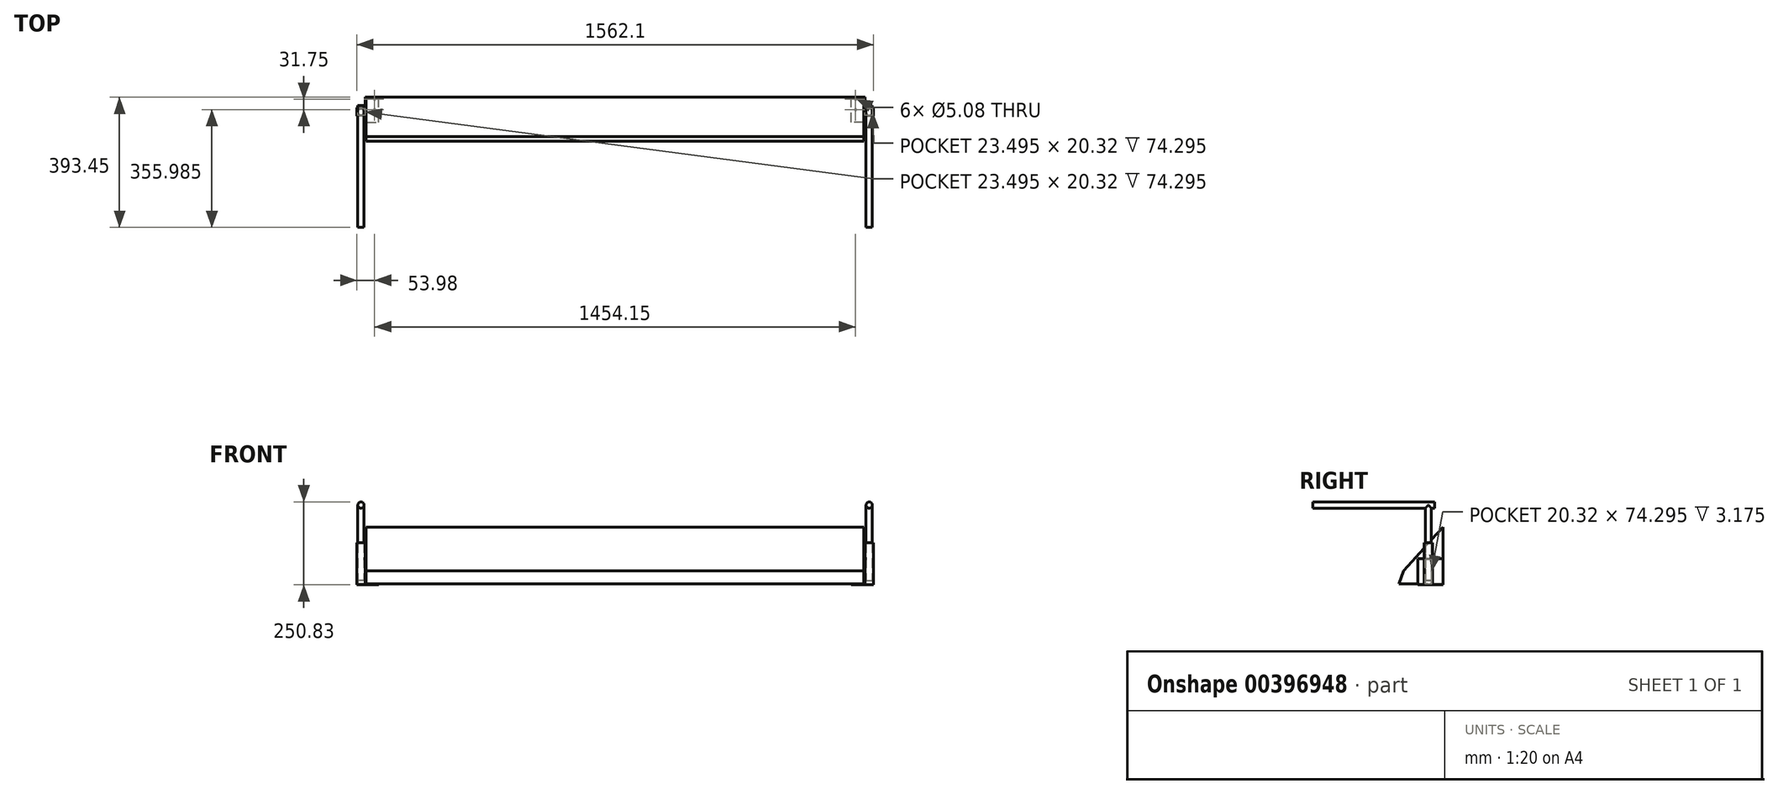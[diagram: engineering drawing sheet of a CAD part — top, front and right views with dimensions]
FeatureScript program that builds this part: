
annotation { "Feature Type Name" : "Feature", "Feature Type Description" : "" }
export const myFeature = defineFeature(function(context is Context, id is Id, definition is map)
    precondition{}
    {
        {
            var Q0;
            Q0=qCreatedBy(makeId("Right.planeOp"),FACE);
            var sketch = newSketch(context, id + "F0", { "sketchPlane" : qUnion([Q0])});
            skLineSegment(sketch, "E0", {"start": v(0, 0) * mm, "end": v(0, 171.45) * mm});
            skLineSegment(sketch, "E1", {"start": v(0, 0) * mm, "end": v(-133.35, 0) * mm});
            skLineSegment(sketch, "E2", {"start": v(-133.35, 0) * mm, "end": v(-119.18, 39.5) * mm});
            skLineSegment(sketch, "E3", {"start": v(-119.18, 39.5) * mm, "end": v(0, 171.45) * mm});
            skSolve(sketch);
        }
        {
            var Q0;
            Q0=makeQuery(id+"F0.imprint","IMPRINT",FACE,{"disambiguationData":[TD([[makeQuery(id+"F0.imprint","IMPRINT",EDGE,{"derivedFrom":sQuery(id+"F0.wireOp",EDGE,"E0")}),1.0]])]});
            extrude(context, id + "F1", {"entities" : qUnion([Q0]), "oppositeDirection" : true, "depth" : 1504.95 * mm});
        }
        {
            var Q0;
            Q0=makeQuery(id+"F1.opExtrude","SWEPT_FACE",FACE,{"disambiguationData":[OSD([sQuery(id+"F0.wireOp",EDGE,"E1")])]});
            var sketch = newSketch(context, id + "F2", { "sketchPlane" : qUnion([Q0])});
            skCircle(sketch, "E4", {"center": v(-1479.55, 37.46) * mm, "radius": 2.54 * mm});
            skCircle(sketch, "E5", {"center": v(-1479.55, 5.72) * mm, "radius": 2.54 * mm});
            skLineSegment(sketch, "E6.bottom", {"start": v(-1504.95, 76.2) * mm, "end": v(-1466.85, 76.2) * mm});
            skLineSegment(sketch, "E6.top", {"start": v(-1504.95, 0) * mm, "end": v(-1466.85, 0) * mm});
            skLineSegment(sketch, "E6.left", {"start": v(-1504.95, 76.2) * mm, "end": v(-1504.95, 0) * mm});
            skLineSegment(sketch, "E6.right", {"start": v(-1466.85, 76.2) * mm, "end": v(-1466.85, 0) * mm});
            skLineSegment(sketch, "E7", {"start": v(-752.48, 133.35) * mm, "end": v(-752.48, 0) * mm, "construction": true});
            skLineSegment(sketch, "E8.MirrorCS", {"start": v(-38.1, 76.2) * mm, "end": v(-38.1, 0) * mm});
            skLineSegment(sketch, "E9.MirrorCS", {"start": v(0, 76.2) * mm, "end": v(-38.1, 76.2) * mm});
            skCircle(sketch, "E10.MirrorC", {"center": v(-25.4, 37.47) * mm, "radius": 2.54 * mm});
            skCircle(sketch, "E11.MirrorC", {"center": v(-25.4, 5.72) * mm, "radius": 2.54 * mm});
            skLineSegment(sketch, "E12.bottom", {"start": v(-1504.95, 76.2) * mm, "end": v(-1508.13, 76.2) * mm});
            skLineSegment(sketch, "E12.top", {"start": v(-1504.95, 0) * mm, "end": v(-1508.13, 0) * mm});
            skLineSegment(sketch, "E12.right", {"start": v(-1508.13, 76.2) * mm, "end": v(-1508.13, 0) * mm});
            skLineSegment(sketch, "E13.MirrorCS", {"start": v(3.17, 76.2) * mm, "end": v(3.17, 0) * mm});
            skLineSegment(sketch, "E14.MirrorCS", {"start": v(0, 0) * mm, "end": v(3.17, 0) * mm});
            skLineSegment(sketch, "E15.MirrorCS", {"start": v(0, 76.2) * mm, "end": v(3.17, 76.2) * mm});
            skSolve(sketch);
        }
        {
            var Q0;
            {var subQ4=sQuery(id+"F2.wireOp",EDGE,"E8.MirrorCS");Q0=makeQuery(id+"F2.imprint","IMPRINT",FACE,{"disambiguationData":[TD([[makeQuery(id+"F2.imprint","IMPRINT",EDGE,{"derivedFrom":subQ4}),1.0]])]});}
            var Q1;
            Q1=makeQuery(id+"F2.imprint","IMPRINT",FACE,{"disambiguationData":[TD([[makeQuery(id+"F2.imprint","IMPRINT",EDGE,{"derivedFrom":sQuery(id+"F2.wireOp",EDGE,"E13.MirrorCS")}),-1.0]])]});
            var Q2;
            Q2=makeQuery(id+"F2.imprint","IMPRINT",FACE,{"disambiguationData":[TD([[makeQuery(id+"F2.imprint","IMPRINT",EDGE,{"derivedFrom":sQuery(id+"F2.wireOp",EDGE,"E4")}),-1.0]])]});
            var Q3;
            Q3=makeQuery(id+"F2.imprint","IMPRINT",FACE,{"disambiguationData":[TD([[makeQuery(id+"F2.imprint","IMPRINT",EDGE,{"derivedFrom":sQuery(id+"F2.wireOp",EDGE,"E12.bottom")}),1.0]])]});
            extrude(context, id + "F3", {"entities" : qUnion([Q0, Q1, Q2, Q3]), "depth" : 3.17 * mm});
        }
        {
            var Q0;
            Q0=makeQuery(id+"F3.opExtrude","CAP_FACE",FACE,{"disambiguationData":[OSD([sQuery(id+"F2.wireOp",EDGE,"E4"),sQuery(id+"F2.wireOp",EDGE,"E5"),sQuery(id+"F2.wireOp",EDGE,"E6.bottom"),sQuery(id+"F2.wireOp",EDGE,"E6.top"),sQuery(id+"F2.wireOp",EDGE,"E6.right"),sQuery(id+"F2.wireOp",EDGE,"E12.bottom"),sQuery(id+"F2.wireOp",EDGE,"E12.top"),sQuery(id+"F2.wireOp",EDGE,"E12.right")])],"isStart":true});
            var sketch = newSketch(context, id + "F4", { "sketchPlane" : qUnion([Q0])});
            skLineSegment(sketch, "E16.bottom", {"start": v(-1508.13, 0) * mm, "end": v(-1504.95, 0) * mm});
            skLineSegment(sketch, "E16.top", {"start": v(-1508.13, -76.2) * mm, "end": v(-1504.95, -76.2) * mm});
            skLineSegment(sketch, "E16.left", {"start": v(-1508.13, 0) * mm, "end": v(-1508.13, -76.2) * mm});
            skLineSegment(sketch, "E16.right", {"start": v(-1504.95, 0) * mm, "end": v(-1504.95, -76.2) * mm});
            skLineSegment(sketch, "E17.bottom", {"start": v(3.17, 0) * mm, "end": v(0, 0) * mm});
            skLineSegment(sketch, "E17.top", {"start": v(3.17, -76.2) * mm, "end": v(0, -76.2) * mm});
            skLineSegment(sketch, "E17.left", {"start": v(3.17, 0) * mm, "end": v(3.17, -76.2) * mm});
            skLineSegment(sketch, "E17.right", {"start": v(0, 0) * mm, "end": v(0, -76.2) * mm});
            skSolve(sketch);
        }
        {
            var Q0;
            Q0 = qSketchRegion(id + "F4", true);
            extrude(context, id + "F5", {"entities" : qUnion([Q0]), "depth" : 76.2 * mm});
        }
        {
            var Q0;
            Q0=makeQuery(id+"F3.opExtrude","SWEPT_BODY",BODY,{"disambiguationData":[OSD([sQuery(id+"F0.wireOp",EDGE,"E0"),sQuery(id+"F0.wireOp",EDGE,"E1"),sQuery(id+"F2.wireOp",EDGE,"E8.MirrorCS"),sQuery(id+"F2.wireOp",EDGE,"E9.MirrorCS"),sQuery(id+"F2.wireOp",EDGE,"E10.MirrorC"),sQuery(id+"F2.wireOp",EDGE,"E11.MirrorC"),sQuery(id+"F2.wireOp",EDGE,"E13.MirrorCS"),sQuery(id+"F2.wireOp",EDGE,"E14.MirrorCS"),sQuery(id+"F2.wireOp",EDGE,"E15.MirrorCS")])]});
            var Q1;
            Q1=makeQuery(id+"F5.opExtrude","SWEPT_BODY",BODY,{"disambiguationData":[OSD([sQuery(id+"F4.wireOp",EDGE,"E17.bottom"),sQuery(id+"F4.wireOp",EDGE,"E17.top"),sQuery(id+"F4.wireOp",EDGE,"E17.left"),sQuery(id+"F4.wireOp",EDGE,"E17.right")])]});
            booleanBodies(context, id + "F6", {"operationType" : BooleanOperationType.UNION, "tools" : qUnion([Q0, Q1])});
        }
        {
            var Q0;
            Q0=makeQuery(id+"F3.opExtrude","CAP_FACE",FACE,{"disambiguationData":[OSD([sQuery(id+"F0.wireOp",EDGE,"E0"),sQuery(id+"F0.wireOp",EDGE,"E1"),sQuery(id+"F2.wireOp",EDGE,"E8.MirrorCS"),sQuery(id+"F2.wireOp",EDGE,"E9.MirrorCS"),sQuery(id+"F2.wireOp",EDGE,"E10.MirrorC"),sQuery(id+"F2.wireOp",EDGE,"E11.MirrorC"),sQuery(id+"F2.wireOp",EDGE,"E13.MirrorCS"),sQuery(id+"F2.wireOp",EDGE,"E14.MirrorCS"),sQuery(id+"F2.wireOp",EDGE,"E15.MirrorCS")])],"isStart":false});
            var sketch = newSketch(context, id + "F7", { "sketchPlane" : qUnion([Q0])});
            skLineSegment(sketch, "E18.bottom", {"start": v(3.17, 57.15) * mm, "end": v(28.57, 57.15) * mm});
            skLineSegment(sketch, "E18.top", {"start": v(3.17, 31.75) * mm, "end": v(28.57, 31.75) * mm});
            skLineSegment(sketch, "E18.left", {"start": v(3.17, 57.15) * mm, "end": v(3.17, 31.75) * mm});
            skLineSegment(sketch, "E18.right", {"start": v(28.57, 57.15) * mm, "end": v(28.57, 31.75) * mm});
            skSolve(sketch);
        }
        {
            var Q0;
            Q0 = qSketchRegion(id + "F7", true);
            extrude(context, id + "F8", {"entities" : qUnion([Q0]), "operationType" : NewBodyOperationType.ADD, "oppositeDirection" : true, "depth" : 127 * mm});
        }
        {
            var Q0;
            Q0=makeQuery(id+"F8.opExtrude","CAP_FACE",FACE,{"disambiguationData":[OSD([sQuery(id+"F7.wireOp",EDGE,"E18.bottom"),sQuery(id+"F7.wireOp",EDGE,"E18.top"),sQuery(id+"F7.wireOp",EDGE,"E18.left"),sQuery(id+"F7.wireOp",EDGE,"E18.right")])],"isStart":false});
            shell(context, id + "F9", {"entities" : qUnion([Q0]), "thickness" : 2.54 * mm});
        }
        {
            var Q0;
            {var subQ0=sQuery(id+"F2.wireOp",EDGE,"E13.MirrorCS");var subQ1=sQuery(id+"F7.wireOp",EDGE,"E18.top");Q0=makeQuery(id+"F8.boolean.opBoolean","SPLIT",EDGE,{"disambiguationData":[topologyDisambiguationEdgeConnected([makeQuery(id+"F3.opExtrude","SWEPT_FACE",FACE,{"disambiguationData":[OSD([subQ0])]})])],"derivedFrom":makeQuery(id+"F8.opExtrude","SWEPT_EDGE",EDGE,{"disambiguationData":[OSD([subQ0,subQ1,sQuery(id+"F7.wireOp",EDGE,"E18.left")])]})});}
            var Q1;
            {var subQ0=sQuery(id+"F2.wireOp",EDGE,"E13.MirrorCS");var subQ1=sQuery(id+"F7.wireOp",EDGE,"E18.bottom");Q1=makeQuery(id+"F8.boolean.opBoolean","SPLIT",EDGE,{"disambiguationData":[topologyDisambiguationEdgeConnected([makeQuery(id+"F3.opExtrude","SWEPT_FACE",FACE,{"disambiguationData":[OSD([subQ0])]})])],"derivedFrom":makeQuery(id+"F8.opExtrude","SWEPT_EDGE",EDGE,{"disambiguationData":[OSD([subQ0,subQ1,sQuery(id+"F7.wireOp",EDGE,"E18.left")])]})});}
            fillet(context, id + "F10", {"entities" : qUnion([Q0, Q1]), "radius" : 5.08 * mm, "tangentPropagation" : true, "allowEdgeOverflow" : false});
        }
        {
            var Q0;
            Q0=makeQuery(id+"F1.opExtrude","CAP_FACE",FACE,{"disambiguationData":[OSD([sQuery(id+"F0.wireOp",EDGE,"E0"),sQuery(id+"F0.wireOp",EDGE,"E1"),sQuery(id+"F0.wireOp",EDGE,"E2"),sQuery(id+"F0.wireOp",EDGE,"E3")])],"isStart":true});
            cPlane(context, id + "F11", {"entities" : qUnion([Q0]), "cplaneType" : CPlaneType.OFFSET, "offset" : 752.47 * mm, "oppositeDirection" : true, "width" : 152.4 * mm, "height" : 152.4 * mm});
        }
        {
            var Q0;
            Q0=makeQuery(id+"F3.opExtrude","SWEPT_BODY",BODY,{"disambiguationData":[OSD([sQuery(id+"F0.wireOp",EDGE,"E0"),sQuery(id+"F0.wireOp",EDGE,"E1"),sQuery(id+"F2.wireOp",EDGE,"E8.MirrorCS"),sQuery(id+"F2.wireOp",EDGE,"E9.MirrorCS"),sQuery(id+"F2.wireOp",EDGE,"E10.MirrorC"),sQuery(id+"F2.wireOp",EDGE,"E11.MirrorC"),sQuery(id+"F2.wireOp",EDGE,"E13.MirrorCS"),sQuery(id+"F2.wireOp",EDGE,"E14.MirrorCS"),sQuery(id+"F2.wireOp",EDGE,"E15.MirrorCS")])]});
            var Q1;
            Q1=qCreatedBy(id+"F11.planeOp",FACE);
            mirror(context, id + "F12", {"entities" : qUnion([Q0]), "mirrorPlane" : qUnion([Q1])});
        }
        {
            var Q0;
            Q0=makeQuery(id+"F12.opPattern","COPY",FACE,{"derivedFrom":makeQuery(id+"F8.opExtrude","CAP_FACE",FACE,{"disambiguationData":[OSD([sQuery(id+"F7.wireOp",EDGE,"E18.bottom"),sQuery(id+"F7.wireOp",EDGE,"E18.top"),sQuery(id+"F7.wireOp",EDGE,"E18.left"),sQuery(id+"F7.wireOp",EDGE,"E18.right")])],"isStart":false}),"instanceName":"1"});
            var sketch = newSketch(context, id + "F13", { "sketchPlane" : qUnion([Q0])});
            skCircle(sketch, "E19", {"center": v(-1520.82, -44.45) * mm, "radius": 9.53 * mm});
            skPoint(sketch, "E19.centerSnap0", {"position": v(-1520.82, -54.61) * mm});
            skPoint(sketch, "E19.centerSnap1", {"position": v(-1530.98, -44.45) * mm});
            skSolve(sketch);
        }
        {
            var Q0;
            Q0 = qSketchRegion(id + "F13", true);
            extrude(context, id + "F14", {"entities" : qUnion([Q0]), "depth" : 127 * mm, "hasSecondDirection" : true, "secondDirectionOppositeDirection" : true, "secondDirectionDepth" : 114.3 * mm});
        }
        {
            var Q0;
            Q0=makeQuery(id+"F12.opPattern","COPY",FACE,{"derivedFrom":makeQuery(id+"F8.opExtrude","SWEPT_FACE",FACE,{"disambiguationData":[OSD([sQuery(id+"F7.wireOp",EDGE,"E18.right")])]}),"instanceName":"1"});
            var sketch = newSketch(context, id + "F15", { "sketchPlane" : qUnion([Q0])});
            skLineSegment(sketch, "E20", {"start": v(31.75, 250.83) * mm, "end": v(82.55, 200.03) * mm});
            skLineSegment(sketch, "E21", {"start": v(82.55, 200.03) * mm, "end": v(31.75, 200.03) * mm});
            skLineSegment(sketch, "E22", {"start": v(31.75, 200.03) * mm, "end": v(31.75, 250.83) * mm});
            skLineSegment(sketch, "E23", {"start": v(31.75, 250.83) * mm, "end": v(82.55, 250.83) * mm});
            skLineSegment(sketch, "E24", {"start": v(82.55, 250.83) * mm, "end": v(82.55, 200.03) * mm});
            skSolve(sketch);
        }
        {
            var Q0;
            Q0=makeQuery(id+"F15.imprint","IMPRINT",FACE,{"disambiguationData":[TD([[makeQuery(id+"F15.imprint","IMPRINT",EDGE,{"derivedFrom":sQuery(id+"F15.wireOp",EDGE,"E20")}),1.0]])]});
            extrude(context, id + "F16", {"entities" : qUnion([Q0]), "operationType" : NewBodyOperationType.REMOVE, "oppositeDirection" : true, "depth" : 25.4 * mm});
        }
        {
            var Q0;
            Q0=makeQuery(id+"F12.opPattern","COPY",FACE,{"derivedFrom":makeQuery(id+"F8.opExtrude","SWEPT_FACE",FACE,{"disambiguationData":[OSD([sQuery(id+"F7.wireOp",EDGE,"E18.bottom")])]}),"instanceName":"1"});
            var sketch = newSketch(context, id + "F17", { "sketchPlane" : qUnion([Q0])});
            skCircle(sketch, "E25", {"center": v(-1520.82, 238.13) * mm, "radius": 9.53 * mm});
            skSolve(sketch);
        }
        {
            var Q0;
            Q0 = qSketchRegion(id + "F17", true);
            extrude(context, id + "F18", {"entities" : qUnion([Q0]), "operationType" : NewBodyOperationType.ADD, "depth" : 336.3 * mm, "hasSecondDirection" : true, "secondDirectionOppositeDirection" : true, "secondDirectionDepth" : 31.75 * mm});
        }
        {
            var Q0;
            Q0=makeQuery(id+"F14.opExtrude","SWEPT_BODY",BODY,{"disambiguationData":[OSD([sQuery(id+"F13.wireOp",EDGE,"E19")])]});
            var Q1;
            Q1=qCreatedBy(id+"F11.planeOp",FACE);
            mirror(context, id + "F19", {"entities" : qUnion([Q0]), "mirrorPlane" : qUnion([Q1])});
        }
    });
